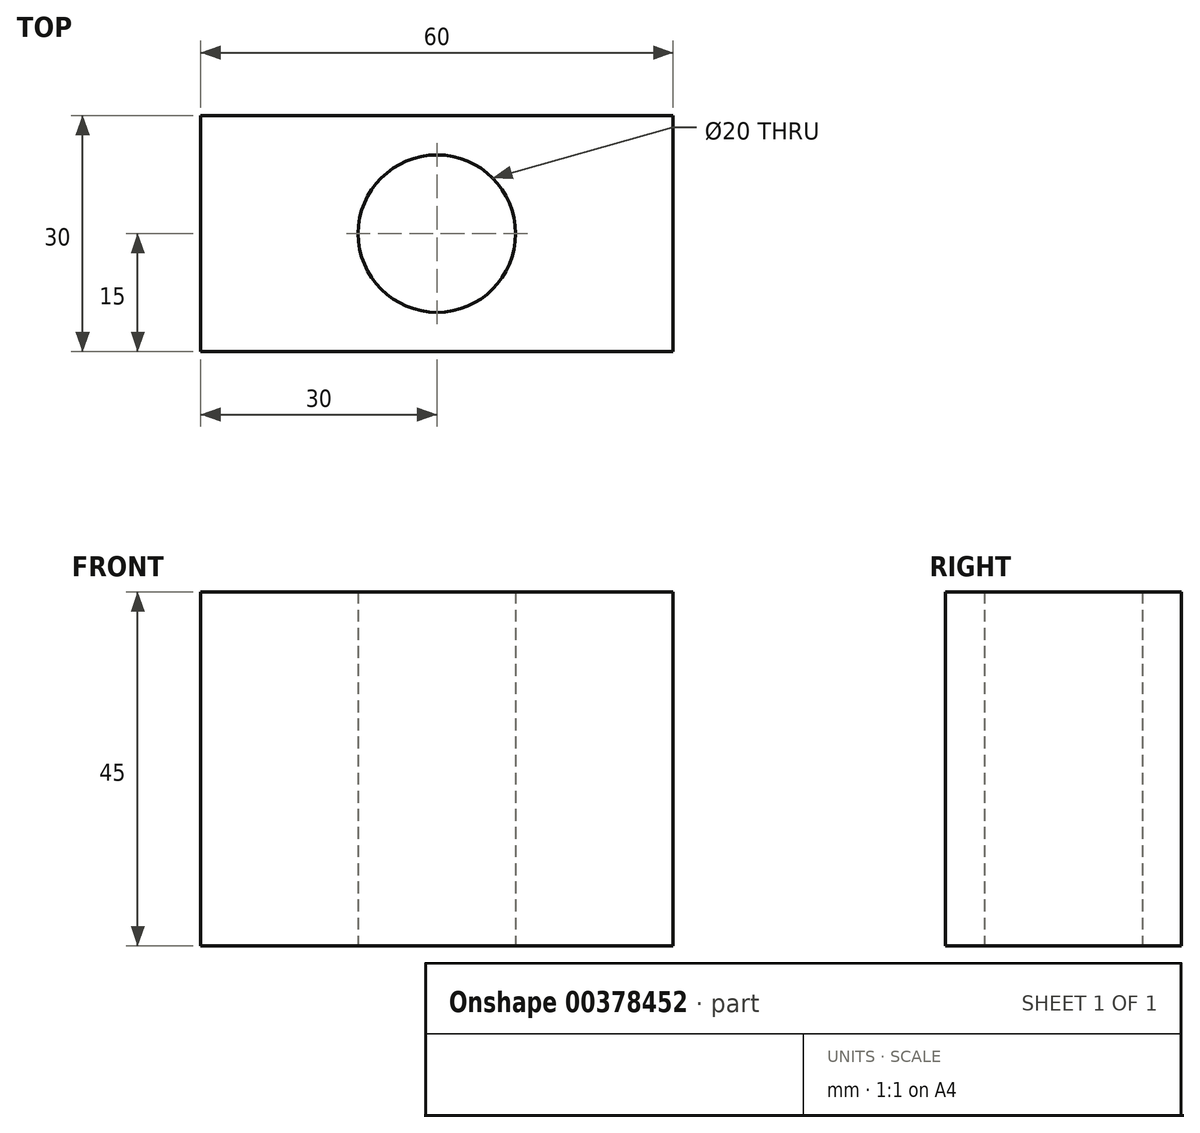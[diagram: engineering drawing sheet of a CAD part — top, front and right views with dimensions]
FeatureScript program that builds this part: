
annotation { "Feature Type Name" : "Feature", "Feature Type Description" : "" }
export const myFeature = defineFeature(function(context is Context, id is Id, definition is map)
    precondition{}
    {
        {
            var Q0;
            Q0=qCreatedBy(makeId("Top.planeOp"),FACE);
            var sketch = newSketch(context, id + "F0", { "sketchPlane" : qUnion([Q0])});
            skLineSegment(sketch, "E0", {"start": v(-12.5, 30) * mm, "end": v(12.5, 30) * mm});
            skArc(sketch, "E1", {"start": v(12.5, 30) * mm, "mid": v(0, 34.39) * mm, "end": v(-12.5, 30) * mm});
            skLineSegment(sketch, "E2", {"start": v(-12.5, 0) * mm, "end": v(12.5, 0) * mm});
            skArc(sketch, "E3", {"start": v(-12.5, 0) * mm, "mid": v(0, -4.39) * mm, "end": v(12.5, 0) * mm});
            skLineSegment(sketch, "E4", {"start": v(-12.5, 30) * mm, "end": v(-30, 30) * mm});
            skLineSegment(sketch, "E5", {"start": v(-30, 30) * mm, "end": v(-30, 0) * mm});
            skLineSegment(sketch, "E6", {"start": v(-30, 0) * mm, "end": v(30, 0) * mm});
            skLineSegment(sketch, "E7", {"start": v(30, 0) * mm, "end": v(30, 30) * mm});
            skLineSegment(sketch, "E8", {"start": v(30, 30) * mm, "end": v(12.5, 30) * mm});
            skCircle(sketch, "E9", {"center": v(0, 15) * mm, "radius": 10 * mm});
            skPoint(sketch, "E10", {"position": v(10, 15) * mm});
            skPoint(sketch, "E11", {"position": v(-10, 15) * mm});
            skPoint(sketch, "E12", {"position": v(0, 25) * mm});
            skPoint(sketch, "E12.positionSnap0", {"position": v(0, 34.39) * mm});
            skPoint(sketch, "E13", {"position": v(0, 30) * mm});
            skPoint(sketch, "E14", {"position": v(0, 5) * mm});
            skPoint(sketch, "E15", {"position": v(0, 0) * mm});
            skSolve(sketch);
        }
        {
            var Q0;
            Q0=makeQuery(id+"F0.imprint","IMPRINT",FACE,{"disambiguationData":[TD([[makeQuery(id+"F0.imprint","IMPRINT",EDGE,{"derivedFrom":sQuery(id+"F0.wireOp",EDGE,"E0")}),-1.0]])]});
            extrude(context, id + "F1", {"entities" : qUnion([Q0]), "depth" : 45 * mm});
        }
    });
